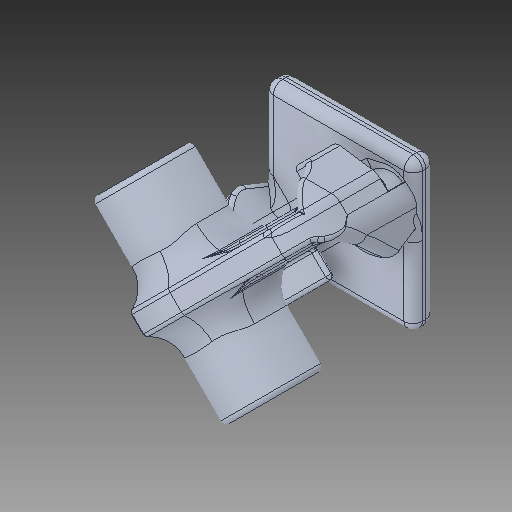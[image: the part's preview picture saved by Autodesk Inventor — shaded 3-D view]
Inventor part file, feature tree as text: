
AUTODESK INVENTOR PART (.ipt)
format: ipt  version: 2018 (Build 220112000, 112)  size: 1,176,576 bytes
history: native  units: in
note: dims shown in document units (in); Inventor stores cm internally (conversion verified against a paired STEP export)
features: fillet x1
ambient origin geometry x8: Origin, YZ Plane, XZ Plane, XY Plane, X Axis, Y Axis, Z Axis, Center Point
bodies: Solid1 (feature_tree)
feature tree (1):
  fillet  "Fillet119"  [1 undecoded]
note: 1 required parameter value undecoded (feature->parameter linkage not recoverable at this tier; creation-order binding heuristic only, values carry confidence <= 0.55)
